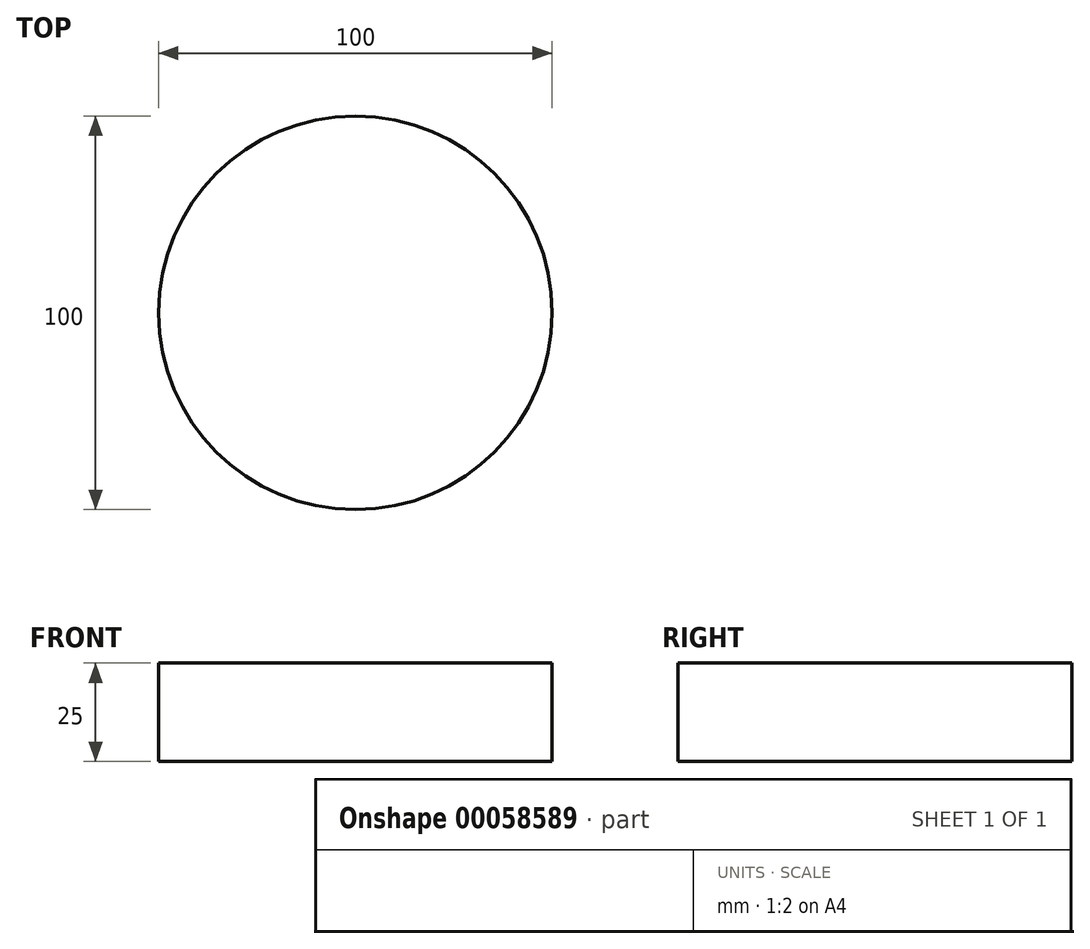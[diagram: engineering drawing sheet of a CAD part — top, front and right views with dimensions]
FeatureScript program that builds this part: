
annotation { "Feature Type Name" : "Feature", "Feature Type Description" : "" }
export const myFeature = defineFeature(function(context is Context, id is Id, definition is map)
    precondition{}
    {
        {
            var Q0;
            Q0=qCreatedBy(makeId("Front.planeOp"),FACE);
            var sketch = newSketch(context, id + "F0", { "sketchPlane" : qUnion([Q0])});
            skLineSegment(sketch, "E0.bottom", {"start": v(0, 0) * mm, "end": v(50, 0) * mm});
            skLineSegment(sketch, "E0.top", {"start": v(0, 25) * mm, "end": v(50, 25) * mm});
            skLineSegment(sketch, "E0.left", {"start": v(0, 0) * mm, "end": v(0, 25) * mm});
            skLineSegment(sketch, "E0.right", {"start": v(50, 0) * mm, "end": v(50, 25) * mm});
            skLineSegment(sketch, "E1", {"start": v(0, 0) * mm, "end": v(0, 109.37) * mm, "construction": true});
            skPoint(sketch, "E1.endSnap0", {"position": v(0, 12.5) * mm});
            skSolve(sketch);
        }
        {
            var Q0;
            Q0=makeQuery(id+"F0.imprint","IMPRINT",FACE,{"disambiguationData":[TD([[makeQuery(id+"F0.imprint","IMPRINT",EDGE,{"derivedFrom":sQuery(id+"F0.wireOp",EDGE,"E0.bottom")}),1.0]])]});
            var Q1;
            Q1=sQuery(id+"F0.wireOp",EDGE,"E1");
            revolve(context, id + "F1", {"entities" : qUnion([Q0]), "axis" : qUnion([Q1]), "revolveType" : RevolveType.FULL});
        }
    });
